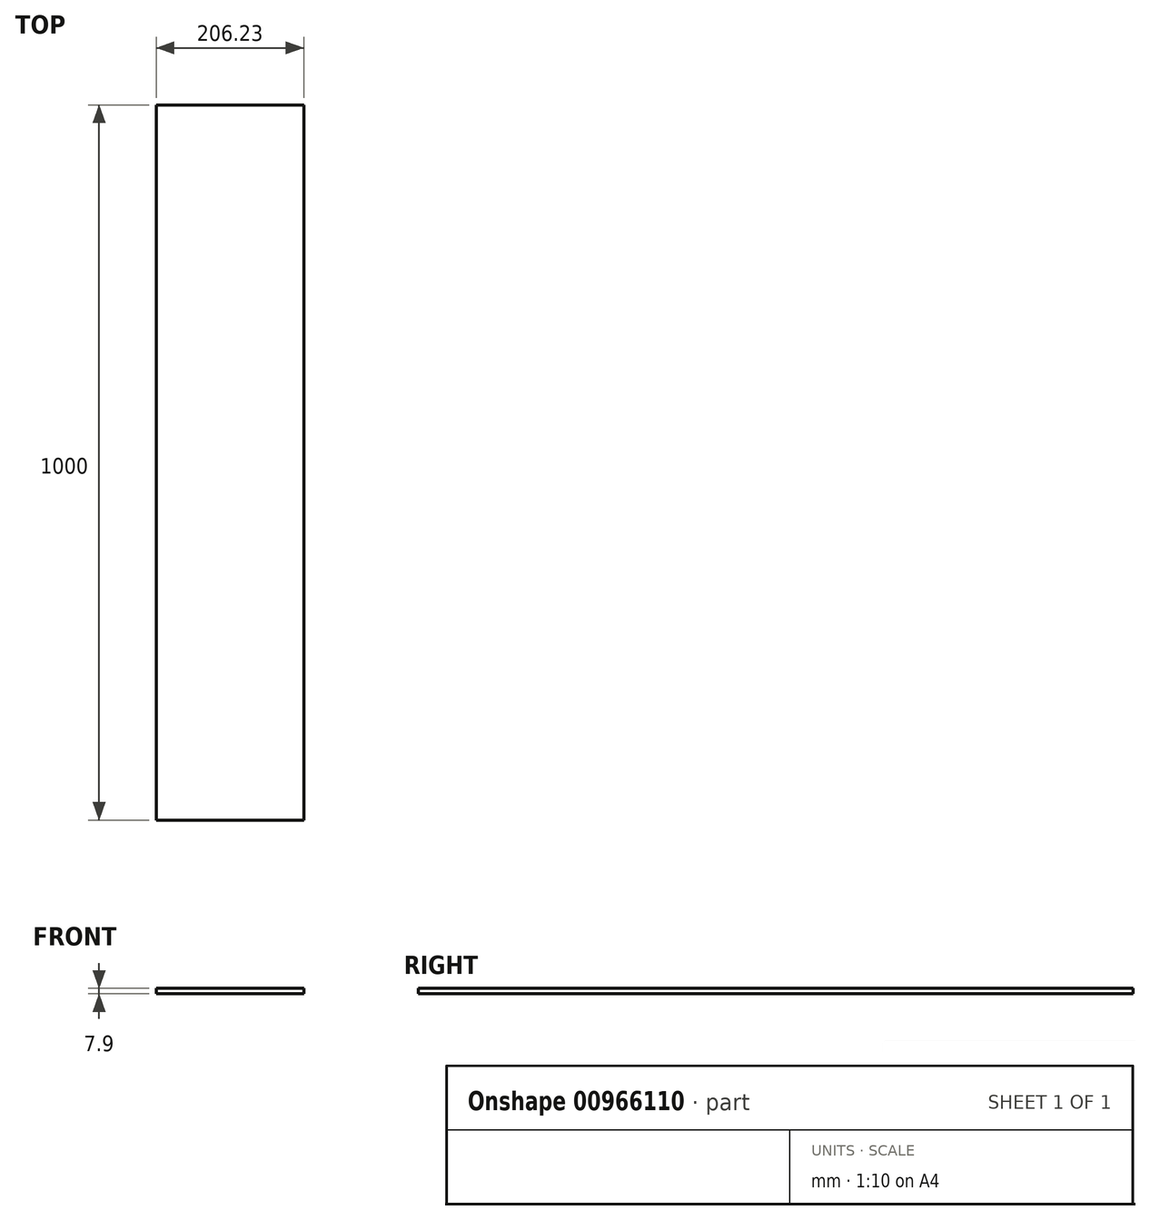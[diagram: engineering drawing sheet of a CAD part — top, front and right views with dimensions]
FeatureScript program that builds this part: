
annotation { "Feature Type Name" : "Feature", "Feature Type Description" : "" }
export const myFeature = defineFeature(function(context is Context, id is Id, definition is map)
    precondition{}
    {
        {
            var Q0;
            Q0=qCreatedBy(makeId("Front.planeOp"),FACE);
            var sketch = newSketch(context, id + "F0", { "sketchPlane" : qUnion([Q0])});
            skLineSegment(sketch, "E0.bottom", {"start": v(-89.09, 111.11) * mm, "end": v(117.14, 111.11) * mm});
            skLineSegment(sketch, "E0.top", {"start": v(-89.09, 103.21) * mm, "end": v(117.14, 103.21) * mm});
            skLineSegment(sketch, "E0.left", {"start": v(-89.09, 111.11) * mm, "end": v(-89.09, 103.21) * mm});
            skLineSegment(sketch, "E0.right", {"start": v(117.14, 111.11) * mm, "end": v(117.14, 103.21) * mm});
            skSolve(sketch);
        }
        {
            var Q0;
            Q0=makeQuery(id+"F0.imprint","IMPRINT",FACE,{"disambiguationData":[TD([[makeQuery(id+"F0.imprint","IMPRINT",EDGE,{"derivedFrom":sQuery(id+"F0.wireOp",EDGE,"E0.bottom")}),-1.0]])]});
            extrude(context, id + "F1", {"entities" : qUnion([Q0]), "depth" : 1000 * mm, "offsetDistance" : 25 * mm});
        }
    });
